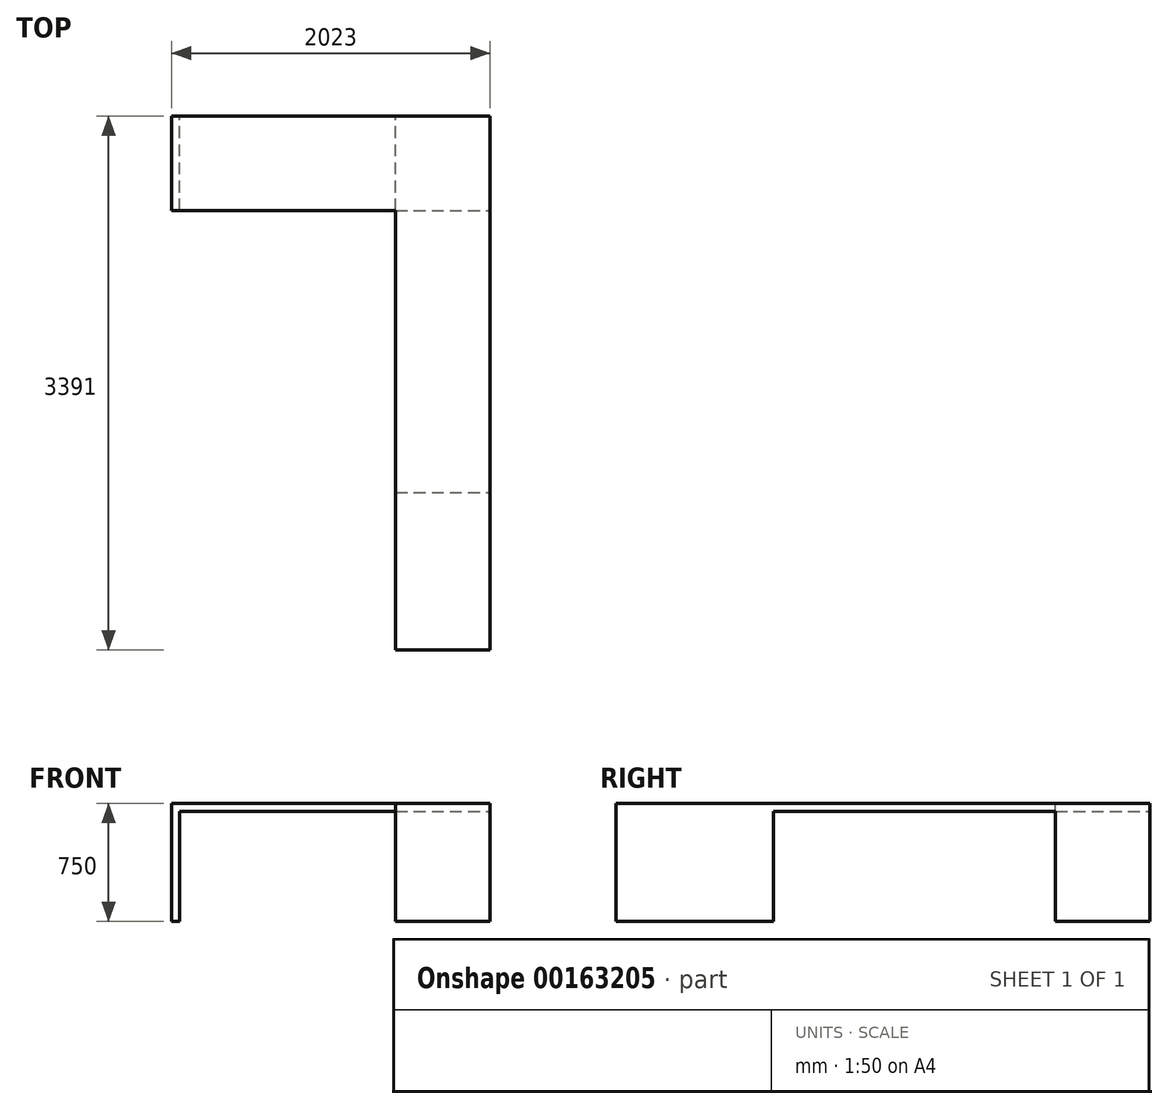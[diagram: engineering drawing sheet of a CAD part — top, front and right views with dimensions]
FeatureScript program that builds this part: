
annotation { "Feature Type Name" : "Feature", "Feature Type Description" : "" }
export const myFeature = defineFeature(function(context is Context, id is Id, definition is map)
    precondition{}
    {
        {
            var Q0;
            Q0=qCreatedBy(makeId("Top.planeOp"),FACE);
            var sketch = newSketch(context, id + "F0", { "sketchPlane" : qUnion([Q0])});
            skLineSegment(sketch, "E0.top", {"start": v(-1423, 0) * mm, "end": v(0, 0) * mm});
            skLineSegment(sketch, "E0.left", {"start": v(-1423, 600) * mm, "end": v(-1423, 0) * mm});
            skLineSegment(sketch, "E1.top", {"start": v(0, -2791) * mm, "end": v(600, -2791) * mm});
            skLineSegment(sketch, "E1.right", {"start": v(600, 600) * mm, "end": v(600, -2791) * mm});
            skLineSegment(sketch, "E2", {"start": v(0, 0) * mm, "end": v(0, -2791) * mm});
            skLineSegment(sketch, "E3", {"start": v(-1423, 600) * mm, "end": v(600, 600) * mm});
            skSolve(sketch);
        }
        {
            var Q0;
            Q0 = qSketchRegion(id + "F0", true);
            extrude(context, id + "F1", {"entities" : qUnion([Q0]), "oppositeDirection" : true, "depth" : 50 * mm});
        }
        {
            var Q0;
            Q0=makeQuery(id+"F1.opExtrude","CAP_FACE",FACE,{"disambiguationData":[OSD([sQuery(id+"F0.wireOp",EDGE,"E0.top"),sQuery(id+"F0.wireOp",EDGE,"E0.left"),sQuery(id+"F0.wireOp",EDGE,"E1.top"),sQuery(id+"F0.wireOp",EDGE,"E1.right"),sQuery(id+"F0.wireOp",EDGE,"E2"),sQuery(id+"F0.wireOp",EDGE,"E3")])],"isStart":false});
            var sketch = newSketch(context, id + "F2", { "sketchPlane" : qUnion([Q0])});
            skLineSegment(sketch, "E4.bottom", {"start": v(-1423, 0) * mm, "end": v(-1373, 0) * mm});
            skLineSegment(sketch, "E4.top", {"start": v(-1423, -600) * mm, "end": v(-1373, -600) * mm});
            skLineSegment(sketch, "E4.left", {"start": v(-1423, 0) * mm, "end": v(-1423, -600) * mm});
            skLineSegment(sketch, "E4.right", {"start": v(-1373, 0) * mm, "end": v(-1373, -600) * mm});
            skLineSegment(sketch, "E5.bottom", {"start": v(0, 0) * mm, "end": v(600, 0) * mm});
            skLineSegment(sketch, "E5.top", {"start": v(0, -600) * mm, "end": v(600, -600) * mm});
            skLineSegment(sketch, "E5.left", {"start": v(0, 0) * mm, "end": v(0, -600) * mm});
            skLineSegment(sketch, "E5.right", {"start": v(600, 0) * mm, "end": v(600, -600) * mm});
            skLineSegment(sketch, "E6.bottom", {"start": v(0, 2791) * mm, "end": v(600, 2791) * mm});
            skLineSegment(sketch, "E6.top", {"start": v(0, 1791) * mm, "end": v(600, 1791) * mm});
            skLineSegment(sketch, "E6.left", {"start": v(0, 2791) * mm, "end": v(0, 1791) * mm});
            skLineSegment(sketch, "E6.right", {"start": v(600, 2791) * mm, "end": v(600, 1791) * mm});
            skSolve(sketch);
        }
        {
            var Q0;
            Q0 = qSketchRegion(id + "F2", true);
            extrude(context, id + "F3", {"entities" : qUnion([Q0]), "operationType" : NewBodyOperationType.ADD, "depth" : 700 * mm});
        }
    });
